# Revit family: Shower-Valve_Trim-KALLISTA-Town-P22713-1
name_source: partatom
category: Specialty Equipment
units: mm (PartAtom-declared; Revit-internal decimal feet)

## family parameters
Cut with Voids When Loaded = No
Host = Face
Maintain Annotation Orientation = No
OmniClass Number = 23.31.25.00
Part Type = Normal
Room Calculation Point = No
Round Connector Dimension = Use Diameter
Shared = No

## types (5) — shared parameters
ADA Compliant = Yes
Assembly Code = C1030200
Date Modified = 04/30/2025
Default Elevation = 42"
Height = 4"
Length = 3 3/8"
Manufacturer = Kallista Co.
Master Format 2014 = 10 28 00
Master Format 2014 Name = Toilet, Bath, and Laundry Accessories
Material = Premium Metal Construction
Product Documentation Link = https://techcomm.kohler.com
Product Name = Town
URL = https://www.kallista.com
WaterSense Certified = No
Width = 4"

## per-type parameters (varying)
| type | Cross Handle | Description | Distance | Finish | Handle Clearance | Lever Handle | Model | Product Page URL | Type |
| Cross Handle, AD-Nickel Silver | Yes | Volume Control Trim ,Cross Handle | 1 1/2" | Kallista-Metal-AD-Nickel_Silver | 3" | No | P22713-CR-AD | https://www.kallista.com | 1 |
| Cross Handle, AG-Brushed Nickel | Yes | Volume Control Trim ,Cross Handle | 1 1/2" | Kallista-Metal-AG-Brushed_Nickel | 3" | No | P22713-CR-AG |  | 2 |
| Cross Handle, CP-Chrome | Yes | Volume Control Trim ,Cross Handle | 1 1/2" | Kallista-Metal-CP-Chrome | 3" | No | P22713-CR-CP | https://www.kallista.com | 3 |
| Lever Handle, AD-Nickel Silver | No | Volume Control Trim, Lever Handle | 0" | Kallista-Metal-AD-Nickel_Silver | 2 3/4" | Yes | P22713-LV-AD | https://www.kallista.com | 4 |
| Lever Handle, CP-Chrome | No | Volume Control Trim, Lever Handle | 0" | Kallista-Metal-CP-Chrome | 2 3/4" | Yes | P22713-LV-CP | https://www.kallista.com | 5 |

## geometry (parser evidence)
native form markers: Sweep x7
no freeform markers — native parametric forms only
